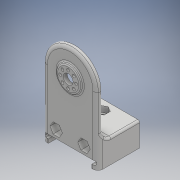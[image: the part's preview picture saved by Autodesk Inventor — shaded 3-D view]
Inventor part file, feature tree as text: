
AUTODESK INVENTOR PART (.ipt)
format: ipt  version: 2018 (Build 220112000, 112)  size: 1,480,704 bytes
history: native  units: mm
features: sketch x11, extrude x10, fillet x7, projected_geometry x5, hole x2, chamfer x2
ambient origin geometry x8: Origin, YZ Plane, XZ Plane, XY Plane, X Axis, Y Axis, Z Axis, Center Point
bodies: Solid1 (feature_tree)
feature tree (37):
  extrude  "Extrusion1"  Depth=1.0mm
  sketch  "Sketch2"  dims[d0=20.5mm d1=0.0mm d2=1.0mm]
  extrude  "Extrusion2"  Depth=56.0mm
  extrude  "Extrusion3"  Depth=44.0mm
  hole  "Hole1"  [1 undecoded]
  extrude  "Extrusion4"  Depth=14.0mm
  extrude  "Extrusion5"  Depth=5.4mm
  chamfer  "Chamfer1"  Distance=8.0mm
  sketch  "Sketch6"  dims[d11=14.0mm d12=14.0mm]
  hole  "Hole2"  [1 undecoded]
  extrude  "Extrusion6"  Depth=8.0mm TaperAngle=0.0deg
  fillet  "Fillet1"  Radius=10.0mm
  extrude  "Extrusion7"  Depth=5.4mm
  fillet  "Fillet4"  Radius=6.0mm
  extrude  "Extrusion8"  Depth=10.0mm
  extrude  "Extrusion9"  Depth=16.0mm
  chamfer  "Chamfer2"  Distance=2.9mm
  fillet  "Fillet5"  Radius=80.0mm
  fillet  "Fillet6"  Radius=15.0mm
  fillet  "Fillet7"  Radius=6.0mm
  fillet  "Fillet8"  Radius=10.0mm
  extrude  "Extrusion10"  Depth=1.0mm
  fillet  "Fillet9"  Radius=18.5mm
  sketch  "Sketch3"  dims[d3=250.0mm d4=56.0mm]
  projected_geometry  "Projected Loop1"
  sketch  "Sketch4"  dims[d5=16.0mm d6=44.0mm]
  sketch  "Sketch5"  dims[d7=5.0mm d8=0.0mm d9=42.0mm d10=0.0mm]
  projected_geometry  "Projected Loop2"
  sketch  "Sketch7"  dims[d13=7.0mm d14=6.0mm d15=4.0mm d16=2.0mm d17=90.0deg d18=8.0mm d19=20.594885mm d20=5.4mm d21=8.0mm d22=0.0mm]
  projected_geometry  "Projected Loop3"
  sketch  "Sketch8"  dims[d23=8.0mm d24=6.0mm]
  sketch  "Sketch10"  dims[d25=4.0mm d26=8.0mm d27=0.0mm]
  sketch  "Sketch12"  dims[d28=1.0mm d29=2.0mm d30=45.0deg d31=10.0mm]
  projected_geometry  "Projected Loop6"
  sketch  "Sketch13"  dims[d32=7.0mm d33=6.0mm d34=4.0mm d35=2.0mm d36=90.0deg d37=8.0mm d38=20.594885mm d39=5.4mm d40=6.0mm d41=0.0mm]
  projected_geometry  "Projected Loop7"
  sketch  "Sketch14"  dims[d42=8.0mm d43=10.0mm d44=16.0mm d45=2.9mm d46=80.0mm d48=360.0deg d59=15.0mm d60=6.0mm d61=10.0mm d62=0.0mm d63=1.0mm d68=18.5mm d69=0.0mm d70=2.0mm d71=0.0mm d72=2.0mm d73=2.0mm d74=45.0deg d75=2.0mm d76=0.5mm d77=5.0mm d78=2.0mm d79=60.0mm d80=0.5mm d81=0.0mm d82=0.25mm]
note: 2 required parameter values undecoded (feature->parameter linkage not recoverable at this tier; creation-order binding heuristic only, values carry confidence <= 0.55)
